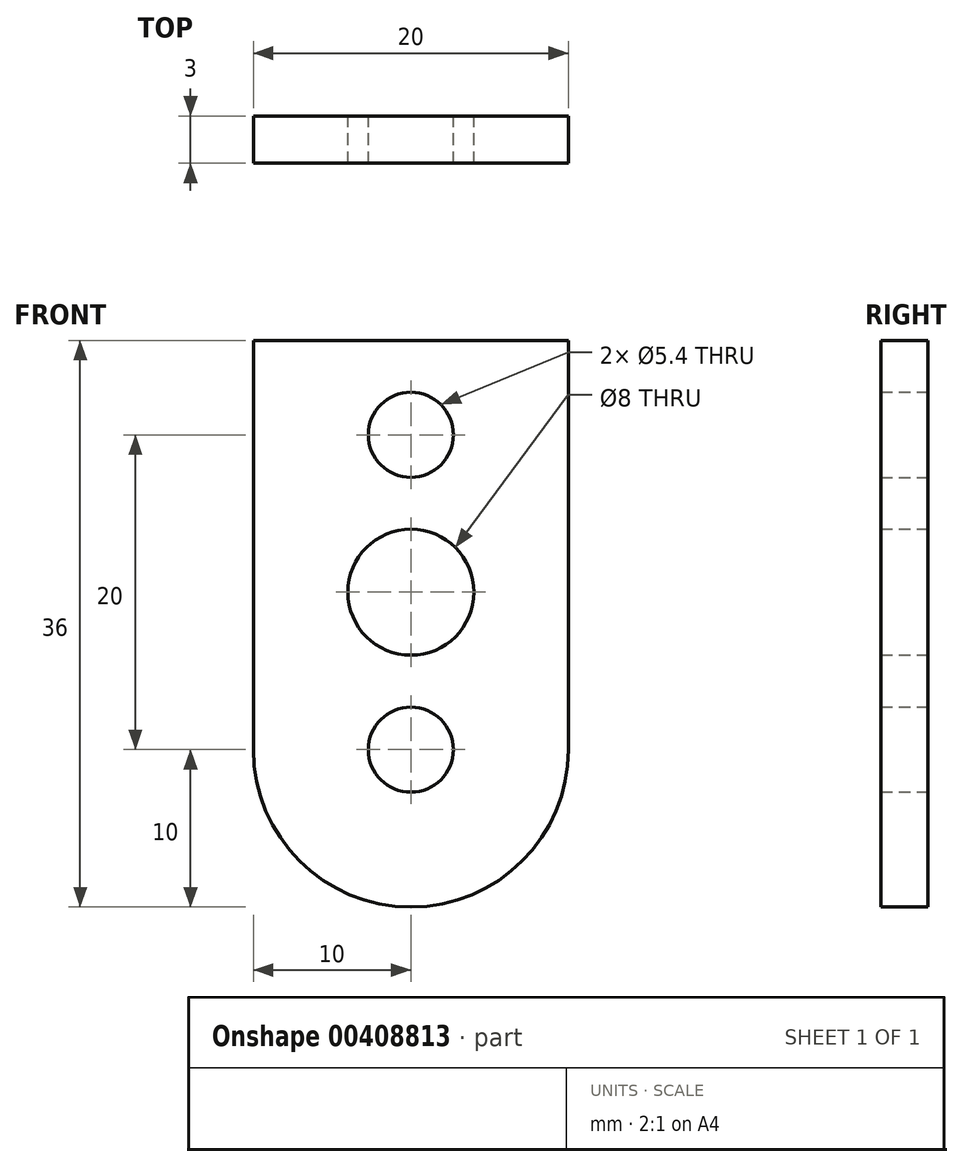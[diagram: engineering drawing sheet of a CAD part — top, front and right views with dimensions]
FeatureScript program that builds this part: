
annotation { "Feature Type Name" : "Feature", "Feature Type Description" : "" }
export const myFeature = defineFeature(function(context is Context, id is Id, definition is map)
    precondition{}
    {
        {
            var Q0;
            Q0=qCreatedBy(makeId("Front.planeOp"),FACE);
            var sketch = newSketch(context, id + "F0", { "sketchPlane" : qUnion([Q0])});
            skLineSegment(sketch, "E0.top", {"start": v(10, 13) * mm, "end": v(-10, 13) * mm});
            skLineSegment(sketch, "E0.left", {"start": v(10, -13) * mm, "end": v(10, 13) * mm});
            skLineSegment(sketch, "E0.right", {"start": v(-10, -13) * mm, "end": v(-10, 13) * mm});
            skPoint(sketch, "E0.middle", {"position": v(0, 0) * mm});
            skArc(sketch, "E1", {"start": v(-10, -13) * mm, "mid": v(0, -23) * mm, "end": v(10, -13) * mm});
            skCircle(sketch, "E2", {"center": v(0, -3) * mm, "radius": 4 * mm});
            skCircle(sketch, "E3", {"center": v(0, 7) * mm, "radius": 2.7 * mm});
            skCircle(sketch, "E4", {"center": v(0, -13) * mm, "radius": 2.7 * mm});
            skSolve(sketch);
        }
        {
            var Q0;
            Q0=makeQuery(id+"F0.imprint","IMPRINT",FACE,{"disambiguationData":[TD([[makeQuery(id+"F0.imprint","IMPRINT",EDGE,{"derivedFrom":sQuery(id+"F0.wireOp",EDGE,"E0.top")}),1.0]])]});
            extrude(context, id + "F1", {"entities" : qUnion([Q0]), "depth" : 3 * mm});
        }
    });
